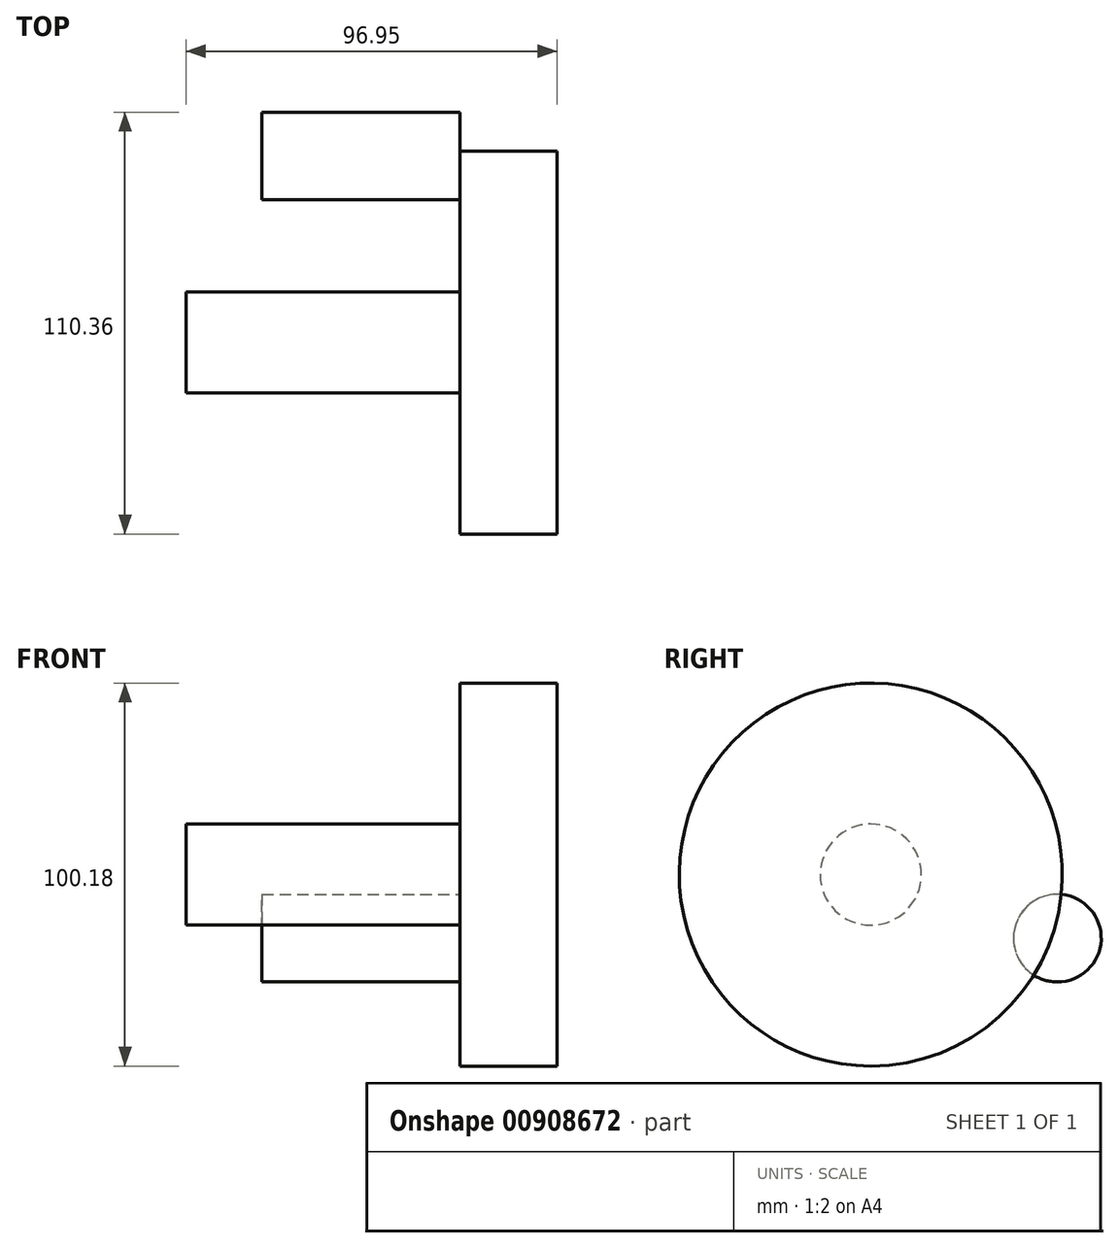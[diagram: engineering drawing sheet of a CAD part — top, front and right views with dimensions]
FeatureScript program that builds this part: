
annotation { "Feature Type Name" : "Feature", "Feature Type Description" : "" }
export const myFeature = defineFeature(function(context is Context, id is Id, definition is map)
    precondition{}
    {
        {
            var Q0;
            Q0=qCreatedBy(makeId("Right.planeOp"),FACE);
            var sketch = newSketch(context, id + "F0", { "sketchPlane" : qUnion([Q0])});
            skCircle(sketch, "E0", {"center": v(0, 0) * mm, "radius": 50.1 * mm});
            skSolve(sketch);
        }
        {
            var Q0;
            Q0=makeQuery(id+"F0.imprint","IMPRINT",FACE,{"disambiguationData":[TD([[makeQuery(id+"F0.imprint","IMPRINT",EDGE,{"derivedFrom":sQuery(id+"F0.wireOp",EDGE,"E0")}),1.0]])]});
            extrude(context, id + "F1", {"entities" : qUnion([Q0]), "depth" : 25.4 * mm, "offsetDistance" : 25.4 * mm});
        }
        {
            var Q0;
            Q0=makeQuery(id+"F1.opExtrude","CAP_FACE",FACE,{"disambiguationData":[OSD([sQuery(id+"F0.wireOp",EDGE,"E0")])],"isStart":false});
            var sketch = newSketch(context, id + "F2", { "sketchPlane" : qUnion([Q0])});
            skCircle(sketch, "E1", {"center": v(0, 0) * mm, "radius": 13.23 * mm});
            skSolve(sketch);
        }
        {
            var Q0;
            Q0 = qSketchRegion(id + "F2", true);
            extrude(context, id + "F3", {"entities" : qUnion([Q0]), "operationType" : NewBodyOperationType.ADD, "oppositeDirection" : true, "depth" : 96.95 * mm, "offsetDistance" : 25.4 * mm});
        }
        {
            var Q0;
            Q0=qCreatedBy(makeId("Right.planeOp"),FACE);
            var sketch = newSketch(context, id + "F4", { "sketchPlane" : qUnion([Q0])});
            skCircle(sketch, "E2", {"center": v(48.8, -16.62) * mm, "radius": 11.47 * mm});
            skSolve(sketch);
        }
        {
            var Q0;
            Q0 = qSketchRegion(id + "F4", true);
            extrude(context, id + "F5", {"entities" : qUnion([Q0]), "operationType" : NewBodyOperationType.ADD, "oppositeDirection" : true, "depth" : 51.74 * mm, "offsetDistance" : 25.4 * mm});
        }
    });
